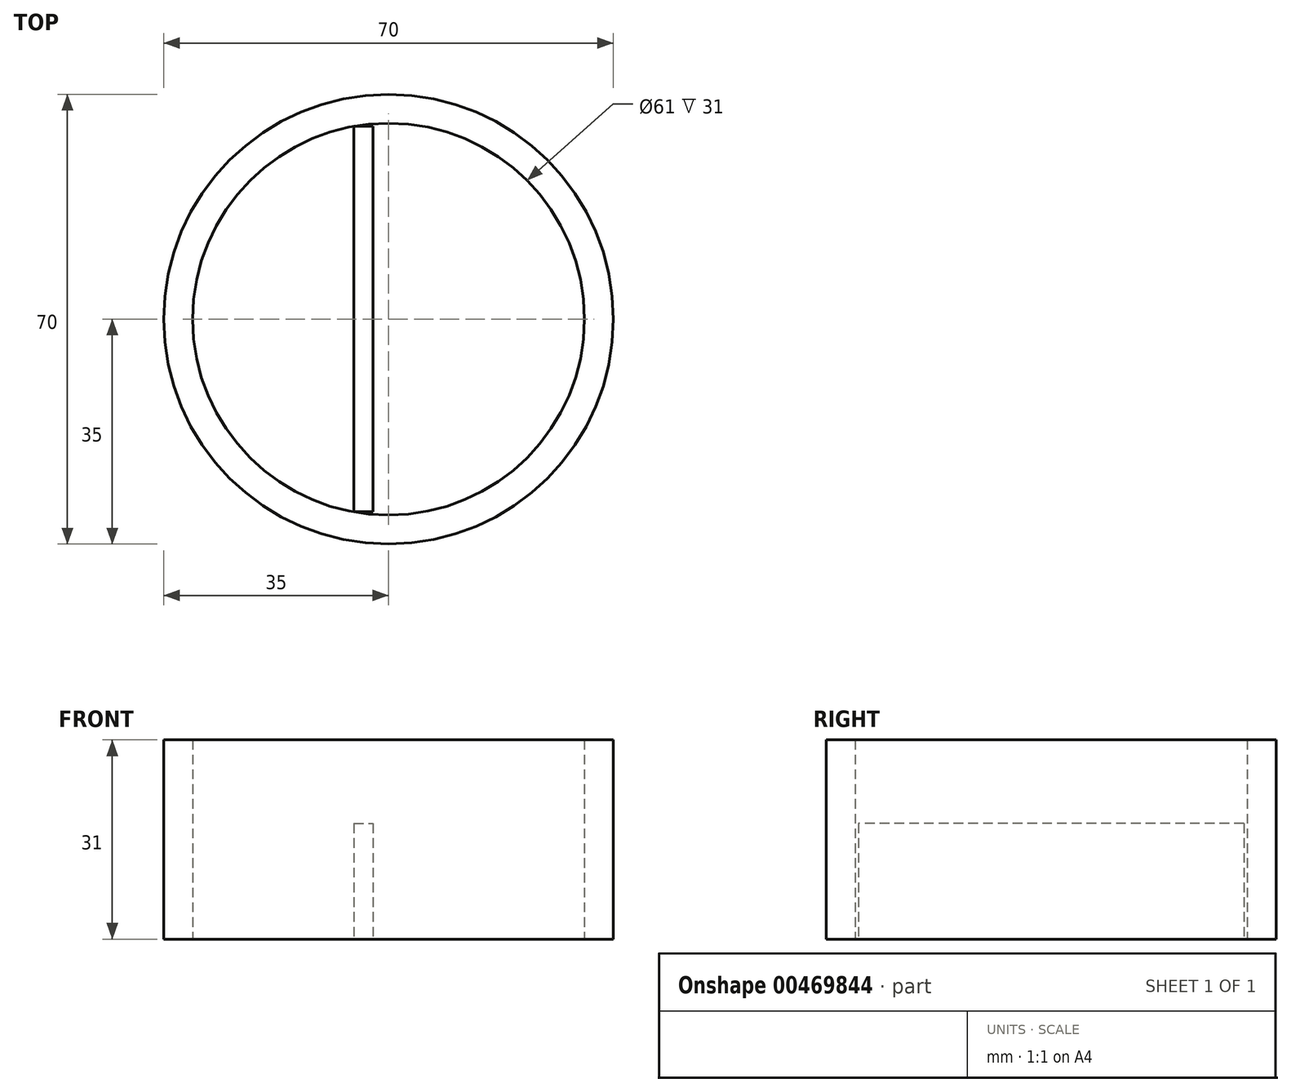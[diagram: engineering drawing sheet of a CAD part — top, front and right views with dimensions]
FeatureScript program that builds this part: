
annotation { "Feature Type Name" : "Feature", "Feature Type Description" : "" }
export const myFeature = defineFeature(function(context is Context, id is Id, definition is map)
    precondition{}
    {
        {
            var Q0;
            Q0=qCreatedBy(makeId("Top.planeOp"),FACE);
            var sketch = newSketch(context, id + "F0", { "sketchPlane" : qUnion([Q0])});
            skCircle(sketch, "E0", {"center": v(0, 0) * mm, "radius": 35 * mm});
            skCircle(sketch, "E1", {"center": v(0, 0) * mm, "radius": 30.5 * mm});
            skSolve(sketch);
        }
        {
            var Q0;
            Q0=makeQuery(id+"F0.imprint","IMPRINT",FACE,{"disambiguationData":[TD([[makeQuery(id+"F0.imprint","IMPRINT",EDGE,{"derivedFrom":sQuery(id+"F0.wireOp",EDGE,"E0")}),1.0]])]});
            extrude(context, id + "F1", {"entities" : qUnion([Q0]), "depth" : 31 * mm});
        }
        {
            var Q0;
            Q0=qCreatedBy(makeId("Top.planeOp"),FACE);
            var sketch = newSketch(context, id + "F2", { "sketchPlane" : qUnion([Q0])});
            skLineSegment(sketch, "E2", {"start": v(-5.4, 0) * mm, "end": v(-5.4, 30.01) * mm});
            skLineSegment(sketch, "E3", {"start": v(-5.4, 0) * mm, "end": v(-5.4, -29.99) * mm});
            skLineSegment(sketch, "E4", {"start": v(5, 0) * mm, "end": v(5, 30.05) * mm});
            skLineSegment(sketch, "E5", {"start": v(5, 30.05) * mm, "end": v(5, -29.95) * mm});
            skPoint(sketch, "E5.endSnap0", {"position": v(5, 15.03) * mm});
            skLineSegment(sketch, "E6", {"start": v(-2.4, 30.01) * mm, "end": v(-2.4, -29.99) * mm});
            skLineSegment(sketch, "E7", {"start": v(2, -29.95) * mm, "end": v(2, 30.05) * mm});
            skLineSegment(sketch, "E8", {"start": v(-5.4, 30.01) * mm, "end": v(-2.4, 30.01) * mm});
            skLineSegment(sketch, "E9", {"start": v(2, 30.05) * mm, "end": v(5, 30.05) * mm});
            skLineSegment(sketch, "E10", {"start": v(-5.4, -29.99) * mm, "end": v(-2.4, -29.99) * mm});
            skLineSegment(sketch, "E11", {"start": v(2, -29.95) * mm, "end": v(5, -29.95) * mm});
            skLineSegment(sketch, "E12", {"start": v(-2.4, -29.99) * mm, "end": v(2, -29.95) * mm});
            skLineSegment(sketch, "E13", {"start": v(-2.4, 30.01) * mm, "end": v(2, 30.05) * mm});
            skSolve(sketch);
        }
        {
            var Q0;
            Q0=makeQuery(id+"F2.imprint","IMPRINT",FACE,{"disambiguationData":[TD([[makeQuery(id+"F2.imprint","IMPRINT",EDGE,{"derivedFrom":sQuery(id+"F2.wireOp",EDGE,"E2")}),-1.0]])]});
            extrude(context, id + "F3", {"entities" : qUnion([Q0]), "depth" : 18 * mm});
        }
    });
